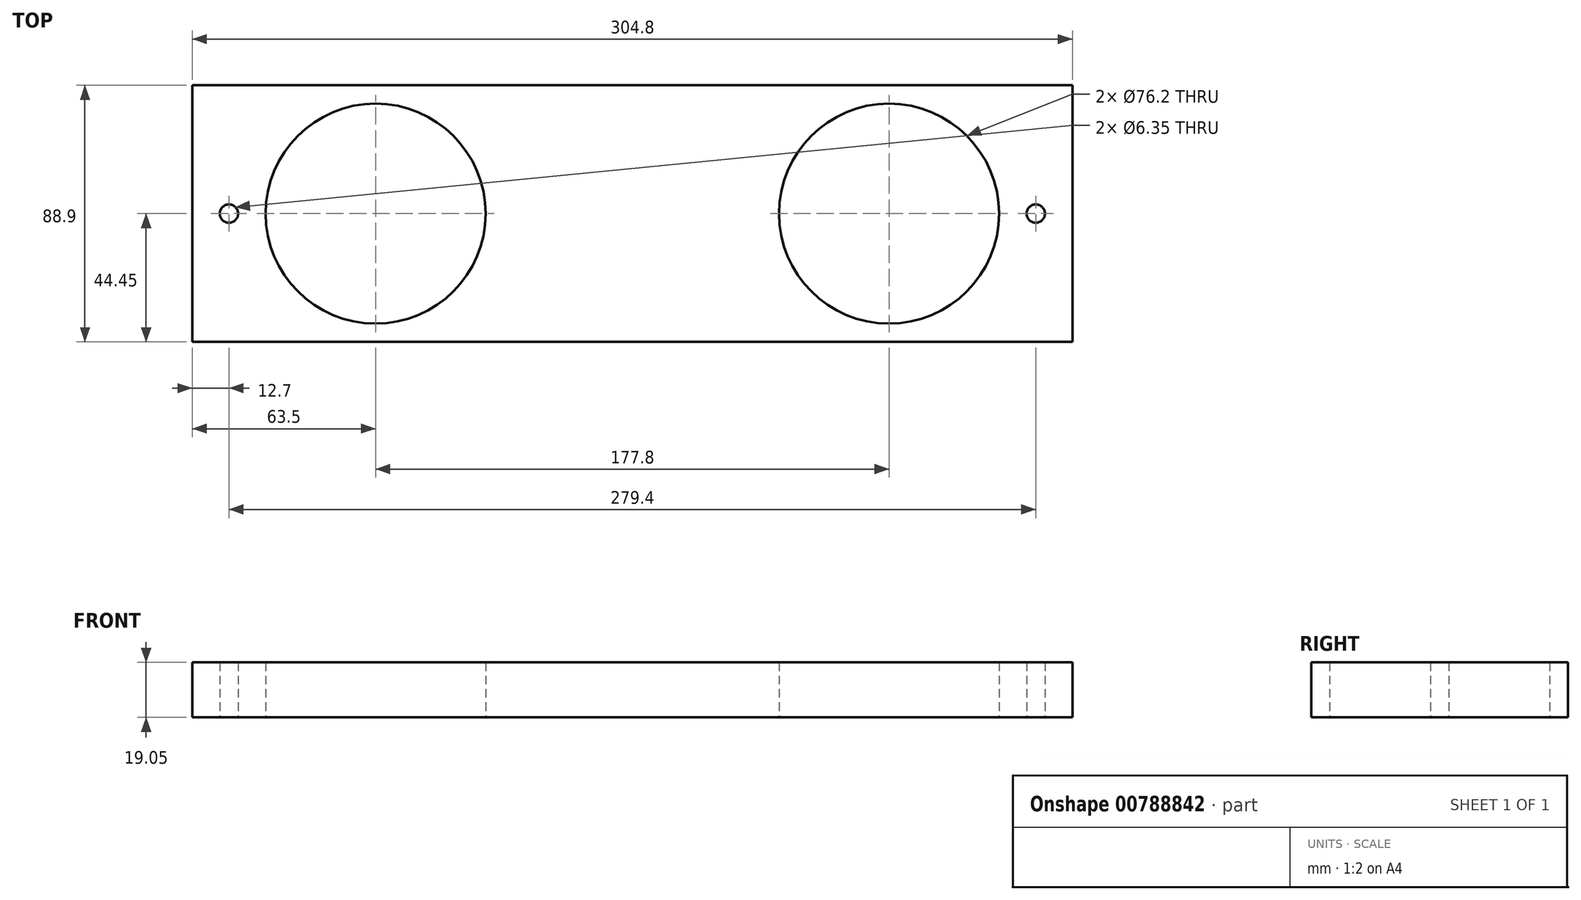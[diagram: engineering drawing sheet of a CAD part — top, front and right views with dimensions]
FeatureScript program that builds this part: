
annotation { "Feature Type Name" : "Feature", "Feature Type Description" : "" }
export const myFeature = defineFeature(function(context is Context, id is Id, definition is map)
    precondition{}
    {
        {
            var Q0;
            Q0=qCreatedBy(makeId("Top.planeOp"),FACE);
            var sketch = newSketch(context, id + "F0", { "sketchPlane" : qUnion([Q0])});
            skLineSegment(sketch, "E0.bottom", {"start": v(-152.4, 88.9) * mm, "end": v(0, 88.9) * mm});
            skLineSegment(sketch, "E0.top", {"start": v(-152.4, 0) * mm, "end": v(0, 0) * mm});
            skLineSegment(sketch, "E0.left", {"start": v(-152.4, 88.9) * mm, "end": v(-152.4, 0) * mm});
            skLineSegment(sketch, "E0.right", {"start": v(0, 88.9) * mm, "end": v(0, 0) * mm});
            skCircle(sketch, "E1", {"center": v(-63.5, 44.45) * mm, "radius": 38.1 * mm});
            skLineSegment(sketch, "E2", {"start": v(0, 44.45) * mm, "end": v(-152.4, 44.45) * mm, "construction": true});
            skSolve(sketch);
        }
        {
            var Q0;
            Q0=makeQuery(id+"F0.imprint","IMPRINT",FACE,{"disambiguationData":[TD([[makeQuery(id+"F0.imprint","IMPRINT",EDGE,{"derivedFrom":sQuery(id+"F0.wireOp",EDGE,"E0.bottom")}),-1.0]])]});
            extrude(context, id + "F1", {"entities" : qUnion([Q0]), "depth" : 19.05 * mm, "offsetDistance" : 25.4 * mm});
        }
        {
            var Q0;
            Q0=makeQuery(id+"F1.opExtrude","SWEPT_BODY",BODY,{"disambiguationData":[OSD([sQuery(id+"F0.wireOp",EDGE,"E0.bottom"),sQuery(id+"F0.wireOp",EDGE,"E0.top"),sQuery(id+"F0.wireOp",EDGE,"E0.left"),sQuery(id+"F0.wireOp",EDGE,"E0.right"),sQuery(id+"F0.wireOp",EDGE,"E1")])]});
            var Q1;
            Q1=makeQuery(id+"F1.opExtrude","SWEPT_FACE",FACE,{"disambiguationData":[OSD([sQuery(id+"F0.wireOp",EDGE,"E0.left")])]});
            mirror(context, id + "F2", {"operationType" : NewBodyOperationType.ADD, "entities" : qUnion([Q0]), "mirrorPlane" : qUnion([Q1])});
        }
        {
            var Q0;
            {var subQ0=makeQuery(id+"F1.opExtrude","CAP_FACE",FACE,{"disambiguationData":[OSD([sQuery(id+"F0.wireOp",EDGE,"E0.bottom"),sQuery(id+"F0.wireOp",EDGE,"E0.top"),sQuery(id+"F0.wireOp",EDGE,"E0.left"),sQuery(id+"F0.wireOp",EDGE,"E0.right"),sQuery(id+"F0.wireOp",EDGE,"E1")])],"isStart":true});Q0=makeQuery(id+"F2.boolean.opBoolean","MERGE",FACE,{"derivedFrom":[subQ0,makeQuery(id+"F2.opPattern","COPY",FACE,{"derivedFrom":subQ0,"instanceName":"1"})]});}
            var sketch = newSketch(context, id + "F3", { "sketchPlane" : qUnion([Q0])});
            skLineSegment(sketch, "E3", {"start": v(-304.8, -44.45) * mm, "end": v(-292.1, -44.45) * mm, "construction": true});
            skLineSegment(sketch, "E4.MirrorCS", {"start": v(0, -44.45) * mm, "end": v(-12.7, -44.45) * mm, "construction": true});
            skSolve(sketch);
        }
        {
            var Q0;
            Q0=sQuery(id+"F3.wireOp",VERTEX,"E3.end");
            var Q1;
            Q1=sQuery(id+"F3.wireOp",VERTEX,"E4.MirrorCS.end");
            var Q2;
            Q2=makeQuery(id+"F1.opExtrude","SWEPT_BODY",BODY,{"disambiguationData":[OSD([sQuery(id+"F0.wireOp",EDGE,"E0.bottom"),sQuery(id+"F0.wireOp",EDGE,"E0.top"),sQuery(id+"F0.wireOp",EDGE,"E0.left"),sQuery(id+"F0.wireOp",EDGE,"E0.right"),sQuery(id+"F0.wireOp",EDGE,"E1")])]});
            hole(context, id + "F4", {"style" : HoleStyle.SIMPLE, "endStyle" : HoleEndStyle.THROUGH, "holeDiameter" : 6.35 * mm, "majorDiameter" : 6.35 * mm, "isTappedThrough" : true, "tappedDepth" : 12.7 * mm, "tapClearance" : 3, "locations" : qUnion([Q0, Q1]), "scope" : qUnion([Q2])});
        }
    });
